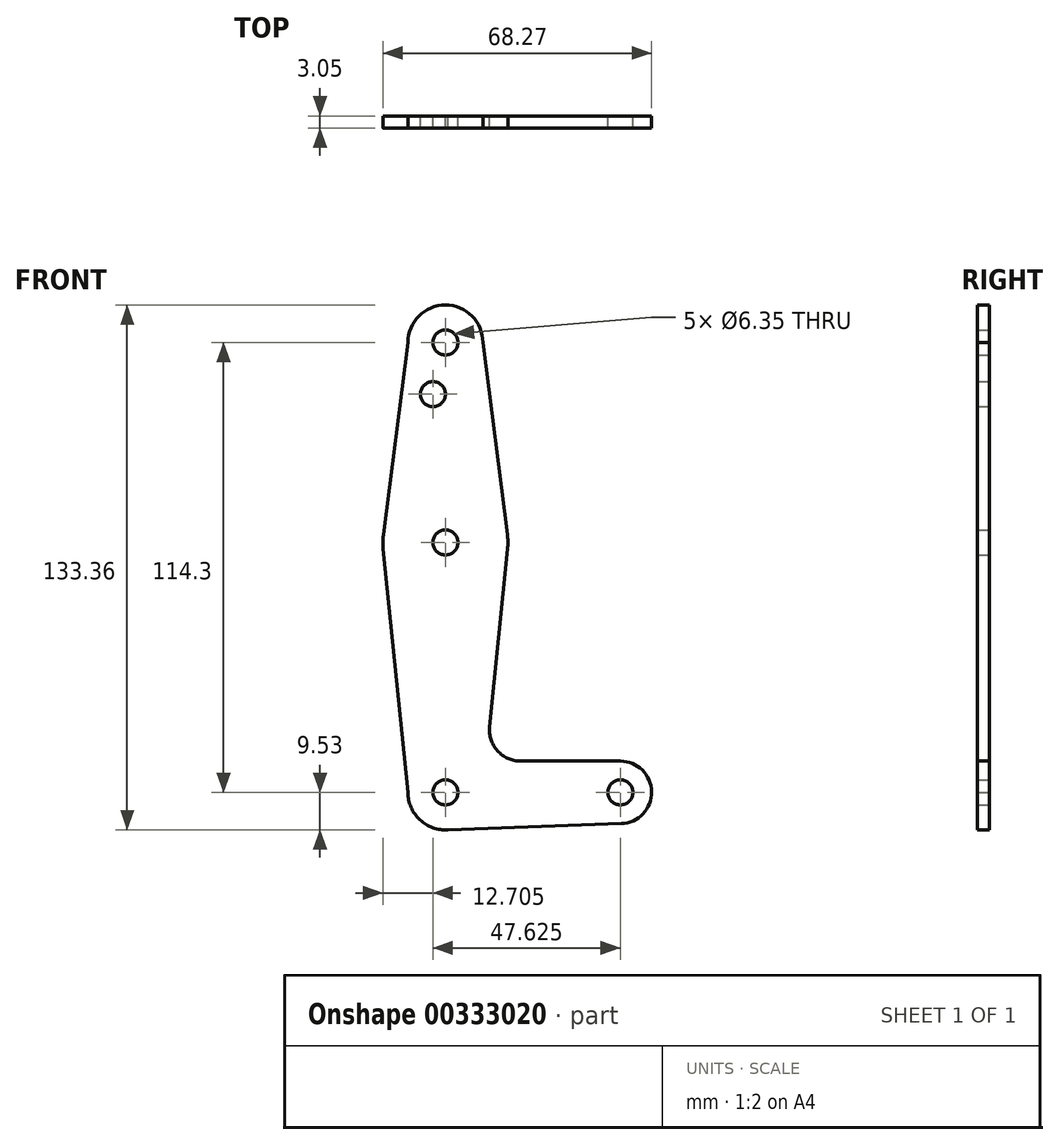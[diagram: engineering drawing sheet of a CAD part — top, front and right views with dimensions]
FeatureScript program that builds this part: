
annotation { "Feature Type Name" : "Feature", "Feature Type Description" : "" }
export const myFeature = defineFeature(function(context is Context, id is Id, definition is map)
    precondition{}
    {
        {
            var Q0;
            Q0=qCreatedBy(makeId("Front.planeOp"),FACE);
            var sketch = newSketch(context, id + "F0", { "sketchPlane" : qUnion([Q0])});
            skLineSegment(sketch, "E0", {"start": v(0, 114.3) * mm, "end": v(0, 0) * mm});
            skLineSegment(sketch, "E1", {"start": v(0, 0) * mm, "end": v(44.45, 0) * mm});
            skCircle(sketch, "E2", {"center": v(0, 0) * mm, "radius": 9.53 * mm});
            skCircle(sketch, "E3", {"center": v(0, 114.3) * mm, "radius": 9.53 * mm});
            skCircle(sketch, "E4", {"center": v(44.45, 0) * mm, "radius": 7.94 * mm});
            skCircle(sketch, "E5", {"center": v(0, 63.5) * mm, "radius": 15.88 * mm});
            skLineSegment(sketch, "E6", {"start": v(-9.52, 114.3) * mm, "end": v(-15.75, 65.5) * mm});
            skLineSegment(sketch, "E7", {"start": v(9.52, 114.3) * mm, "end": v(15.75, 65.5) * mm});
            skLineSegment(sketch, "E8", {"start": v(-9.52, 0) * mm, "end": v(-15.8, 61.9) * mm});
            skLineSegment(sketch, "E9", {"start": v(11.22, 16.69) * mm, "end": v(15.8, 61.9) * mm});
            skLineSegment(sketch, "E10", {"start": v(19.12, 7.94) * mm, "end": v(44.45, 7.94) * mm});
            skLineSegment(sketch, "E11", {"start": v(0, -9.53) * mm, "end": v(44.73, -7.93) * mm});
            skCircle(sketch, "E12", {"center": v(0, 63.5) * mm, "radius": 3.17 * mm});
            skCircle(sketch, "E13", {"center": v(0, 114.3) * mm, "radius": 3.18 * mm});
            skCircle(sketch, "E14", {"center": v(0, 0) * mm, "radius": 3.18 * mm});
            skCircle(sketch, "E15", {"center": v(44.45, 0) * mm, "radius": 3.18 * mm});
            skCircle(sketch, "E16", {"center": v(-3.17, 101.17) * mm, "radius": 3.18 * mm});
            skArc(sketch, "E17.filletArc", {"start": v(11.22, 16.69) * mm, "mid": v(13.23, 10.56) * mm, "end": v(19.12, 7.94) * mm});
            skSolve(sketch);
        }
        {
            var Q0;
            Q0 = qSketchRegion(id + "F0", true);
            var Q1;
            {var subQ0=sQuery(id+"F0.wireOp",EDGE,"E2");var subQ1=sQuery(id+"F0.wireOp",EDGE,"E0");var subQ2=makeQuery(id+"F0.imprint","INTERSECT",VERTEX,{"derivedFrom":[subQ1,subQ0]});Q1=makeQuery(id+"F0.imprint","IMPRINT",FACE,{"disambiguationData":[TD([[makeQuery(id+"F0.imprint","IMPRINT",EDGE,{"disambiguationData":[TD([[subQ2,-1.0]])],"derivedFrom":subQ1}),1.0]])]});}
            extrude(context, id + "F1", {"entities" : qUnion([Q0, Q1]), "depth" : 3.05 * mm});
        }
    });
